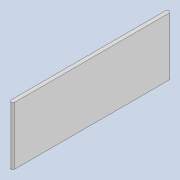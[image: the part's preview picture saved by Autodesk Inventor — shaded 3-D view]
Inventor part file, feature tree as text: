
AUTODESK INVENTOR PART (.ipt)
format: ipt  version: 2020 (Build 240168000, 168)  size: 75,776 bytes
history: native  units: mm
features: extrude x1, sketch x1
ambient origin geometry x8: Origin, YZ Plane, XZ Plane, XY Plane, X Axis, Y Axis, Z Axis, Center Point
bodies: Solid1 (feature_tree)
feature tree (2):
  extrude  "Extrusion1"  Depth=0.2mm
  sketch  "Sketch1"  dims[d0=8.0mm d1=0.2mm d2=3.0mm d3=0.0mm]
